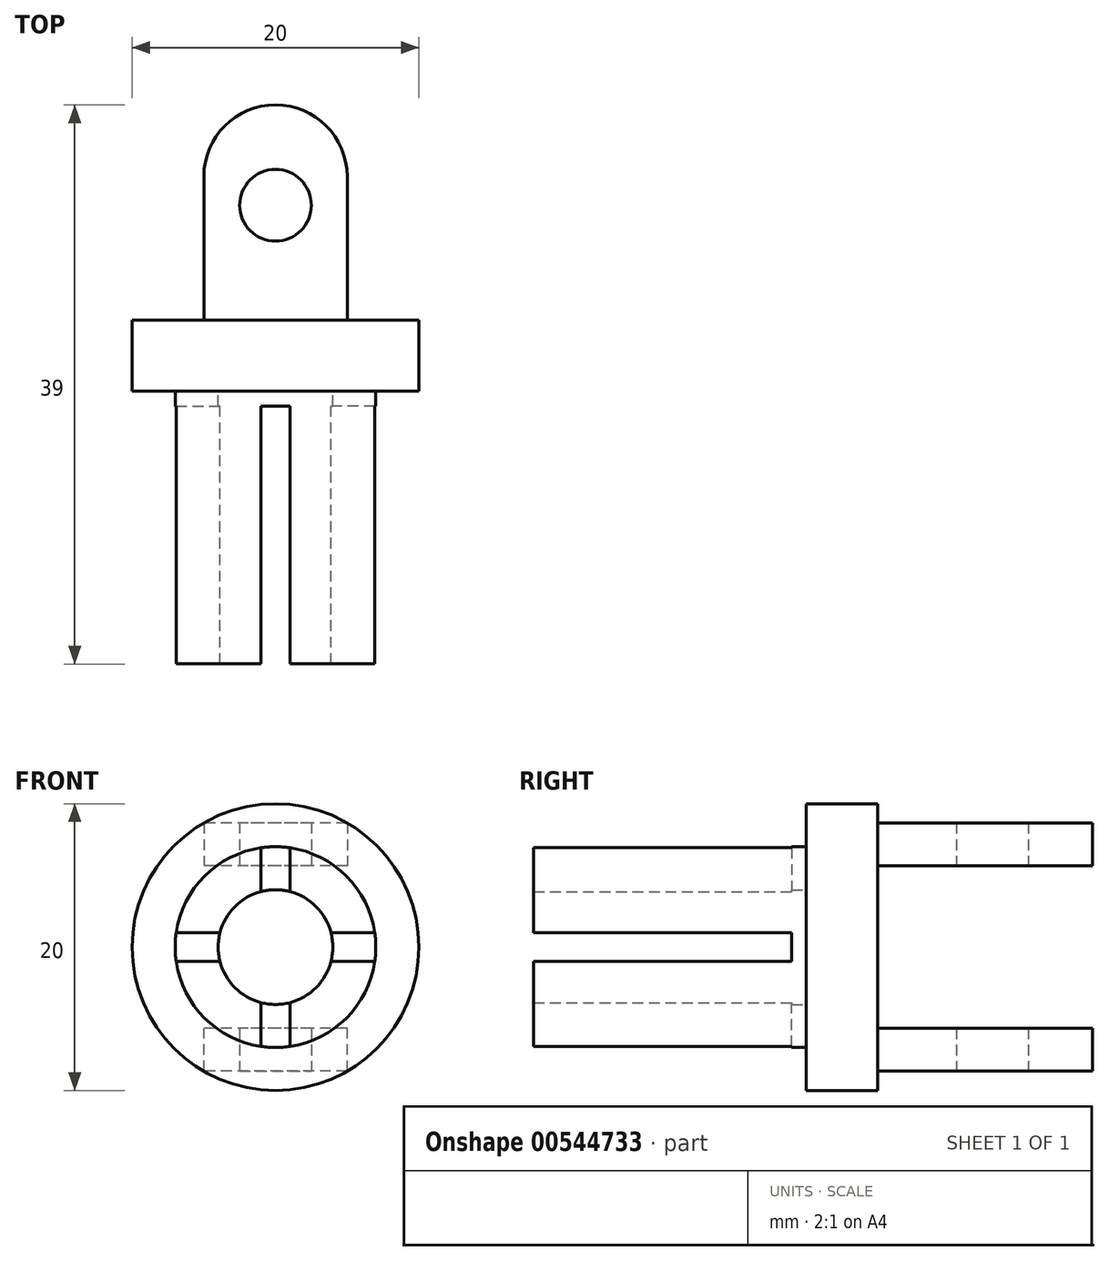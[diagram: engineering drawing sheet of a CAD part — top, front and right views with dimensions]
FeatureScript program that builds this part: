
annotation { "Feature Type Name" : "Feature", "Feature Type Description" : "" }
export const myFeature = defineFeature(function(context is Context, id is Id, definition is map)
    precondition{}
    {
        {
            var Q0;
            Q0=qCreatedBy(makeId("Top.planeOp"),FACE);
            var sketch = newSketch(context, id + "F0", { "sketchPlane" : qUnion([Q0])});
            skLineSegment(sketch, "E0", {"start": v(-10, 9.27) * mm, "end": v(0, 9.27) * mm});
            skLineSegment(sketch, "E1", {"start": v(0, 9.27) * mm, "end": v(0, 4.27) * mm});
            skLineSegment(sketch, "E2", {"start": v(0, 4.27) * mm, "end": v(-4, 4.27) * mm});
            skLineSegment(sketch, "E3", {"start": v(-4, 4.27) * mm, "end": v(-4, -14.73) * mm});
            skLineSegment(sketch, "E4", {"start": v(-4, -14.73) * mm, "end": v(-7, -14.73) * mm});
            skLineSegment(sketch, "E5", {"start": v(-10, 4.3) * mm, "end": v(-7, 4.3) * mm});
            skLineSegment(sketch, "E6", {"start": v(-7, 4.3) * mm, "end": v(-7, -14.73) * mm});
            skLineSegment(sketch, "E7", {"start": v(-10, 4.3) * mm, "end": v(-10, 9.27) * mm});
            skSolve(sketch);
        }
        {
            var Q0;
            Q0=qSketchRegion(id+"F0",true);
            var Q1;
            Q1=sQuery(id+"F0.wireOp",EDGE,"E1");
            revolve(context, id + "F1", {"entities" : qUnion([Q0]), "axis" : qUnion([Q1]), "revolveType" : RevolveType.FULL});
        }
        {
            var Q0;
            Q0=makeQuery(id+"F1.opRevolve","SWEPT_FACE",FACE,{"disambiguationData":[OSD([sQuery(id+"F0.wireOp",EDGE,"E0")])]});
            var sketch = newSketch(context, id + "F2", { "sketchPlane" : qUnion([Q0])});
            skLineSegment(sketch, "E8.bottom", {"start": v(-5, 8.66) * mm, "end": v(5, 8.66) * mm});
            skLineSegment(sketch, "E8.top", {"start": v(-5, 5.66) * mm, "end": v(5, 5.66) * mm});
            skLineSegment(sketch, "E8.left", {"start": v(-5, 8.66) * mm, "end": v(-5, 5.66) * mm});
            skLineSegment(sketch, "E8.right", {"start": v(5, 8.66) * mm, "end": v(5, 5.66) * mm});
            skLineSegment(sketch, "E9.bottom", {"start": v(-5, -8.66) * mm, "end": v(5, -8.66) * mm});
            skLineSegment(sketch, "E9.top", {"start": v(-5, -5.66) * mm, "end": v(5, -5.66) * mm});
            skLineSegment(sketch, "E9.left", {"start": v(-5, -8.66) * mm, "end": v(-5, -5.66) * mm});
            skLineSegment(sketch, "E9.right", {"start": v(5, -8.66) * mm, "end": v(5, -5.66) * mm});
            skSolve(sketch);
        }
        {
            var Q0;
            Q0=makeQuery(id+"F2.imprint","IMPRINT",FACE,{"disambiguationData":[TD([[makeQuery(id+"F2.imprint","IMPRINT",EDGE,{"derivedFrom":sQuery(id+"F2.wireOp",EDGE,"E8.bottom")}),-1.0]])]});
            var Q1;
            Q1=makeQuery(id+"F2.imprint","IMPRINT",FACE,{"disambiguationData":[TD([[makeQuery(id+"F2.imprint","IMPRINT",EDGE,{"derivedFrom":sQuery(id+"F2.wireOp",EDGE,"E9.bottom")}),1.0]])]});
            extrude(context, id + "F3", {"entities" : qUnion([Q0, Q1]), "operationType" : NewBodyOperationType.ADD, "depth" : 15 * mm, "offsetDistance" : 25 * mm});
        }
        {
            var Q0;
            Q0=makeQuery(id+"F3.opExtrude","CAP_EDGE",EDGE,{"disambiguationData":[OSD([sQuery(id+"F2.wireOp",EDGE,"E9.right")])],"isStart":false});
            var Q1;
            Q1=makeQuery(id+"F3.opExtrude","CAP_EDGE",EDGE,{"disambiguationData":[OSD([sQuery(id+"F2.wireOp",EDGE,"E9.left")])],"isStart":false});
            var Q2;
            Q2=makeQuery(id+"F3.opExtrude","CAP_EDGE",EDGE,{"disambiguationData":[OSD([sQuery(id+"F2.wireOp",EDGE,"E8.left")])],"isStart":false});
            var Q3;
            Q3=makeQuery(id+"F3.opExtrude","CAP_EDGE",EDGE,{"disambiguationData":[OSD([sQuery(id+"F2.wireOp",EDGE,"E8.right")])],"isStart":false});
            fillet(context, id + "F4", {"entities" : qUnion([Q0, Q1, Q2, Q3]), "radius" : 5 * mm, "tangentPropagation" : true, "allowEdgeOverflow" : false});
        }
        {
            var Q0;
            Q0=makeQuery(id+"F3.opExtrude","SWEPT_FACE",FACE,{"disambiguationData":[OSD([sQuery(id+"F2.wireOp",EDGE,"E9.bottom")])]});
            var sketch = newSketch(context, id + "F5", { "sketchPlane" : qUnion([Q0])});
            skCircle(sketch, "E10", {"center": v(0, -17.27) * mm, "radius": 2.5 * mm});
            skSolve(sketch);
        }
        {
            var Q0;
            Q0=makeQuery(id+"F5.imprint","IMPRINT",FACE,{"disambiguationData":[TD([[makeQuery(id+"F5.imprint","IMPRINT",EDGE,{"derivedFrom":sQuery(id+"F5.wireOp",EDGE,"E10")}),1.0]])]});
            extrude(context, id + "F6", {"entities" : qUnion([Q0]), "operationType" : NewBodyOperationType.REMOVE, "endBound" : BoundingType.THROUGH_ALL, "oppositeDirection" : true, "depth" : 25 * mm, "offsetDistance" : 25 * mm});
        }
        {
            var Q0;
            Q0=makeQuery(id+"F1.opRevolve","SWEPT_FACE",FACE,{"disambiguationData":[OSD([sQuery(id+"F0.wireOp",EDGE,"E4")])]});
            var sketch = newSketch(context, id + "F7", { "sketchPlane" : qUnion([Q0])});
            skLineSegment(sketch, "E11.bottom", {"start": v(-1, 7.88) * mm, "end": v(1, 7.88) * mm});
            skLineSegment(sketch, "E11.top", {"start": v(-1, 3.08) * mm, "end": v(1, 3.08) * mm});
            skLineSegment(sketch, "E11.left", {"start": v(-1, 7.88) * mm, "end": v(-1, 3.08) * mm});
            skLineSegment(sketch, "E11.right", {"start": v(1, 7.88) * mm, "end": v(1, 3.08) * mm});
            skLineSegment(sketch, "E12.1.0", {"start": v(-7.88, -1) * mm, "end": v(-3.08, -1) * mm});
            skLineSegment(sketch, "E12.1.1", {"start": v(-7.88, -1) * mm, "end": v(-7.88, 1) * mm});
            skLineSegment(sketch, "E12.1.2", {"start": v(-7.88, 1) * mm, "end": v(-3.08, 1) * mm});
            skLineSegment(sketch, "E12.1.3", {"start": v(-3.08, -1) * mm, "end": v(-3.08, 1) * mm});
            skLineSegment(sketch, "E12.2.0", {"start": v(1, -7.88) * mm, "end": v(1, -3.08) * mm});
            skLineSegment(sketch, "E12.2.1", {"start": v(1, -7.88) * mm, "end": v(-1, -7.88) * mm});
            skLineSegment(sketch, "E12.2.2", {"start": v(-1, -7.88) * mm, "end": v(-1, -3.08) * mm});
            skLineSegment(sketch, "E12.2.3", {"start": v(1, -3.08) * mm, "end": v(-1, -3.08) * mm});
            skLineSegment(sketch, "E12.3.0", {"start": v(7.88, 1) * mm, "end": v(3.08, 1) * mm});
            skLineSegment(sketch, "E12.3.1", {"start": v(7.88, 1) * mm, "end": v(7.88, -1) * mm});
            skLineSegment(sketch, "E12.3.2", {"start": v(7.88, -1) * mm, "end": v(3.08, -1) * mm});
            skLineSegment(sketch, "E12.3.3", {"start": v(3.08, 1) * mm, "end": v(3.08, -1) * mm});
            skPoint(sketch, "E12.center", {"position": v(0, 0) * mm});
            skSolve(sketch);
        }
        {
            var Q0;
            Q0 = qSketchRegion(id + "F7", true);
            extrude(context, id + "F8", {"entities" : qUnion([Q0]), "operationType" : NewBodyOperationType.REMOVE, "oppositeDirection" : true, "depth" : 18 * mm, "offsetDistance" : 25 * mm});
        }
    });
